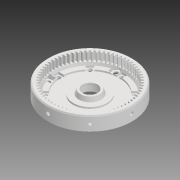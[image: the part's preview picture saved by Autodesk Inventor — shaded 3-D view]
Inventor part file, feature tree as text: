
AUTODESK INVENTOR PART (.ipt)
format: ipt  version: 2020 (Build 240168000, 168)  size: 1,798,656 bytes
history: native  units: mm
features: other x9, extrude x6, sketch x5, pattern_circular x4, revolve x2, chamfer x2, fillet x1, imported_body x1, projected_geometry x1
ambient origin geometry x8: Origin, YZ Plane, XZ Plane, XY Plane, X Axis, Y Axis, Z Axis, Center Point
bodies: Solid1 (feature_tree)
feature tree (31):
  other  "HD_mastersketch.ipt"
  other  "Blocks"
  revolve  "Revolution1"  [1 undecoded]
  extrude  "Extrusion1"  Depth=3.9mm
  extrude  "Extrusion3"  Depth=80.0mm TaperAngle=360.0deg
  pattern_circular  "Circular Pattern1"  [2 undecoded]
  extrude  "Extrusion2"  Depth=1.5mm
  fillet  "Fillet1"  Radius=700.0mm
  pattern_circular  "Circular Pattern2"  [2 undecoded]
  extrude  "Extrusion5"  Depth=1.5mm TaperAngle=0.0deg
  extrude  "Extrusion7"  Depth=1.5mm
  chamfer  "Chamfer1"  Distance=4.3mm
  extrude  "Extrusion8"  TaperAngle=0.0deg  [1 undecoded]
  chamfer  "Chamfer2"  Distance=2.268928mm
  pattern_circular  "Circular Pattern3"  [2 undecoded]
  revolve  "Revolution2"  [1 undecoded]
  pattern_circular  "Circular Pattern4"  Angle=45.0deg  [1 undecoded]
  other  "608 bearing"
  other  "Belt"
  other  "Rotor"
  imported_body  "Base"
  sketch  "Sketch5"  dims[d0=10.0mm d24=7.0mm d25=22.0mm d26=8.0mm]
  other  "M3NutDepth_bot"
  projected_geometry  "Projected Loop1"
  sketch  "Sketch7"  dims[d1=90.0deg d2=3.9mm]
  other  "BeltCutDepth_bot"
  sketch  "Sketch12"  dims[d4=4.0mm d5=0.0mm d6=80.0mm d7=360.0deg]
  sketch  "Sketch13"  dims[d9=0.8mm]
  sketch  "Sketch14"  dims[d11=1.8mm d12=4.0mm d13=0.0mm d14=0.45mm d15=700.0mm d16=360.0deg d18=5.7mm d19=4.0mm d20=0.0mm d29=47.0mm d30=4.3mm d31=0.0mm d32=0.0mm d38=2.268928mm d39=7.2mm d40=1.5mm d41=3.2mm d42=0.0mm d43=0.0mm d44=2.0mm d45=2.0mm d46=45.0deg d47=8.726646mm d48=0.523599mm d49=0.523599mm d50=0.523599mm d51=0.523599mm d52=0.523599mm d53=0.523599mm d56=2.792527mm d57=0.523599mm d58=68.0mm d59=70.740362mm d60=1.780032mm d61=9.749343mm d62=7.969311mm d63=6.189278mm d64=4.409246mm d65=2.629213mm d66=0.523599mm d67=0.523599mm d68=0.523599mm d69=0.523599mm d70=0.523599mm d72=11.529376mm d73=13.309408mm d74=15.089441mm d75=16.869473mm d76=18.649506mm d77=0.523599mm d78=0.523599mm d79=20.429538mm d80=22.209571mm d82=0.250579mm d83=72.932651mm d84=22.5mm d85=15.0mm d86=2.0mm d87=1.0mm d88=0.0mm d89=0.3mm d90=1.0mm d91=45.0deg d92=80.0mm d93=360.0deg d97=7.5mm d98=1.6mm d99=1.4mm d100=2.5mm d101=1.0mm d102=90.0deg d103=80.0mm d104=360.0deg]
  other  "608 bearing:1"
  other  "608 bearing:2"
note: 10 required parameter values undecoded (feature->parameter linkage not recoverable at this tier; creation-order binding heuristic only, values carry confidence <= 0.55)